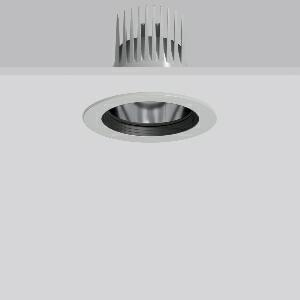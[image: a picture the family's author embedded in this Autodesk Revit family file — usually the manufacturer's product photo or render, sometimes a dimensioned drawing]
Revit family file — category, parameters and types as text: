
# Revit family: heledon_maxi_e_901766_004_76_7b87
name_source: partatom
category: Lighting Fixtures
units: mm (PartAtom-declared; Revit-internal decimal feet)

## family parameters
Cut with Voids When Loaded = No
Host = Face
Light Source = No
Part Type = Normal
Room Calculation Point = No
Round Connector Dimension = Use Diameter
Shared = No

## types (1)
- HELEDON maxi E (1 x LED Modul 930, 4150 lm, 3000)
    Apparent Load = 35 VA
    Approval mark = CE
    CIE Flux Codes = 97 100 100 100 100
    Color Rendering = 90
    Color Temperature = 3000
    Default Elevation = 1800 mm
    Description = Series: HELEDON maxi
Round recessed downlight. Housing: die-cast aluminium, powder-coated. Black plastic ring and recessed LED to prevent glare from the side. Optical assembly with reflector made of MIRO-Silver with 98% total light reflection for outstanding efficiency - can be changed without tools. Best colour rendering index Ra>90. Suitable for Recessed ceiling mounting. Installation without tools thanks to spring fastening system. Including separate LED converter with connecting cable 600 mm.High quality converter without flickering and stroboscopic effect. Through-wiring box (5 pole) available as accessory. The following accessories can be mounted without use of tools: interchangeable lenses, decorative glasses, honeycomb louvre, clear and frosted diffusers, white interchangeable plastic ring. 
Colour: silver
Diameter: 162 mm
Height: 3 mm
Cut-out diameter: 152 mm
Recess height: 200 mm
Luminaire: recess height: 135 mm
Lamp: LED
Socket: without socket
Colour temperature: 3000K
Colour rendering index (CRI): 92
System power: 35 W
Rated luminous flux: 4150 lm
Luminous efficiency: 119 lm/W
Control gear: Converter, dimmable, DALI
Protection class: II
Type of protection: IP 20
    Height = 0 mm  [stored 0 ft]
    Lamp = 1 x LED Modul 930
    Lamp Light Flux = 4150 lm
    Lamp count = 1
    Length = 162 mm
    Lifetime = 50000 h
    Luminous efficacy = 119 lm/W
    Manufacturer = RZB
    ModVariant = No
    Model = 901766.004.76
    Mounting Place = Ceiling
    Mounting Type = Recessed
    Number of Poles = 1
    OnlyDefault = Yes
    Power Factor = 1
    Product Name = HELEDON maxi E
    Product group = Recessed downlights
    ProductGroupID = 402
    Protection Class = Protection class II
    Protection Degree = IP 20
    RLX_Detail_Level = 1
    RLX_Emergency_Light_Flux = 0 lm
    RLX_Emergency_Type = 0
    RLX_Emergency_Type_DB = No
    RlxData = <blob elided: 119453 chars, md5=faea1215>
    Socket = socket
    Standby Power = 0 W
    System Light Flux = 4150 lm
    System Power = 35 W
    Type Comments = Product without accessories
    Type Image = 901662.004.jpg
    URL = http://relux.com
    VarID = ---
    Voltage = 230 V
    Voltage Range = 220-240 V
    Weight = 0.00 kg
    Width = 0 mm  [stored 0 ft]

note: [stored X ft] marks values corroborated as IEEE doubles in the binary element streams (Revit-internal decimal feet)

## geometry (parser evidence)
native form markers: Blend x4, Sweep x10
no freeform markers — native parametric forms only
